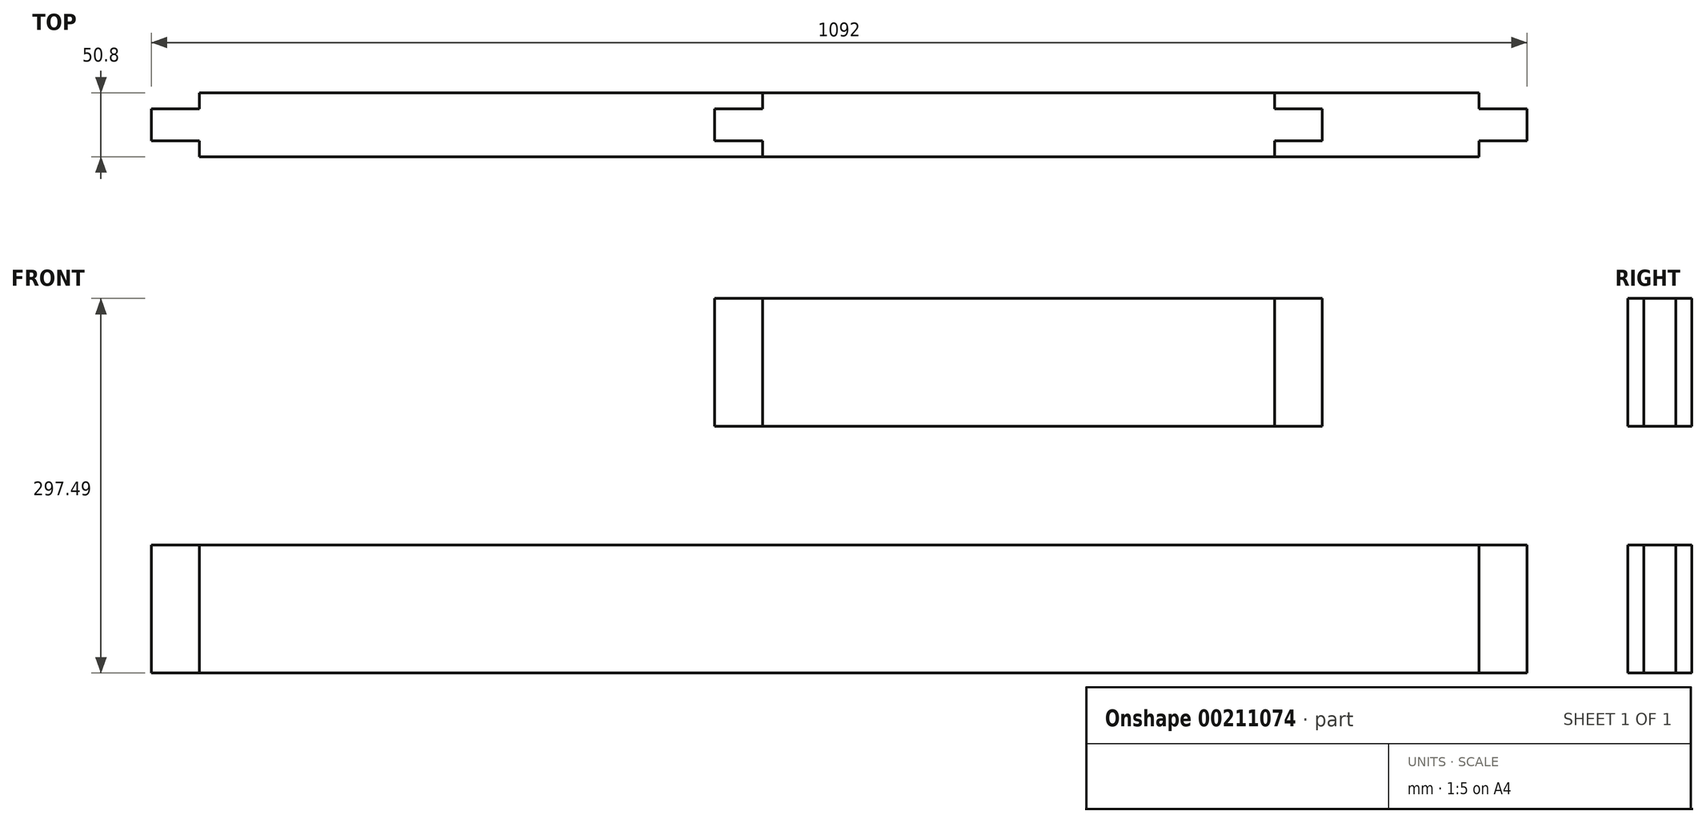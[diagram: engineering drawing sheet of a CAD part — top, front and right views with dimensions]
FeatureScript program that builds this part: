
annotation { "Feature Type Name" : "Feature", "Feature Type Description" : "" }
export const myFeature = defineFeature(function(context is Context, id is Id, definition is map)
    precondition{}
    {
        {
            var Q0;
            Q0=qCreatedBy(makeId("Front.planeOp"),FACE);
            var sketch = newSketch(context, id + "F0", { "sketchPlane" : qUnion([Q0])});
            skLineSegment(sketch, "E0.bottom", {"start": v(365.66, 0) * mm, "end": v(-650.34, 0) * mm});
            skLineSegment(sketch, "E0.top", {"start": v(365.66, 101.6) * mm, "end": v(-650.34, 101.6) * mm});
            skLineSegment(sketch, "E0.left", {"start": v(365.66, 0) * mm, "end": v(365.66, 101.6) * mm});
            skLineSegment(sketch, "E0.right", {"start": v(-650.34, 0) * mm, "end": v(-650.34, 101.6) * mm});
            skLineSegment(sketch, "E1.bottom", {"start": v(203.2, 195.9) * mm, "end": v(-203.2, 195.9) * mm});
            skLineSegment(sketch, "E1.top", {"start": v(203.2, 297.5) * mm, "end": v(-203.2, 297.5) * mm});
            skLineSegment(sketch, "E1.left", {"start": v(203.2, 195.9) * mm, "end": v(203.2, 297.5) * mm});
            skLineSegment(sketch, "E1.right", {"start": v(-203.2, 195.9) * mm, "end": v(-203.2, 297.5) * mm});
            skPoint(sketch, "E1.middle", {"position": v(0, 246.7) * mm});
            skSolve(sketch);
        }
        {
            var Q0;
            Q0=qSketchRegion(id+"F0",true);
            extrude(context, id + "F9", {"entities" : qUnion([Q0]), "depth" : 50.8 * mm});
        }
        {
            var Q0;
            Q0=makeQuery(id+"F9.opExtrude","SWEPT_FACE",FACE,{"disambiguationData":[OSD([sQuery(id+"F0.wireOp",EDGE,"E0.left")])]});
            var sketch = newSketch(context, id + "F1", { "sketchPlane" : qUnion([Q0])});
            skLineSegment(sketch, "E2.bottom", {"start": v(-12.7, 101.6) * mm, "end": v(-38.1, 101.6) * mm});
            skLineSegment(sketch, "E2.top", {"start": v(-12.7, 0) * mm, "end": v(-38.1, 0) * mm});
            skLineSegment(sketch, "E2.left", {"start": v(-12.7, 101.6) * mm, "end": v(-12.7, 0) * mm});
            skLineSegment(sketch, "E2.right", {"start": v(-38.1, 101.6) * mm, "end": v(-38.1, 0) * mm});
            skPoint(sketch, "E2.middle", {"position": v(-25.4, 50.8) * mm});
            skPoint(sketch, "E2.middle.positionSnap0", {"position": v(-25.4, 0) * mm});
            skPoint(sketch, "E2.middle.positionSnap1", {"position": v(0, 50.8) * mm});
            skPoint(sketch, "E2.centerSnap0", {"position": v(-25.4, 0) * mm});
            skPoint(sketch, "E2.centerSnap1", {"position": v(0, 50.8) * mm});
            skSolve(sketch);
        }
        {
            var Q0;
            Q0=makeQuery(id+"F1.imprint","IMPRINT",FACE,{"disambiguationData":[TD([[makeQuery(id+"F1.imprint","IMPRINT",EDGE,{"derivedFrom":sQuery(id+"F1.wireOp",EDGE,"E2.bottom")}),-1.0]])]});
            extrude(context, id + "F2", {"entities" : qUnion([Q0]), "operationType" : NewBodyOperationType.ADD, "depth" : 38 * mm});
        }
        {
            var Q0;
            Q0=makeQuery(id+"F9.opExtrude","SWEPT_FACE",FACE,{"disambiguationData":[OSD([sQuery(id+"F0.wireOp",EDGE,"E0.right")])]});
            var sketch = newSketch(context, id + "F3", { "sketchPlane" : qUnion([Q0])});
            skLineSegment(sketch, "E3.bottom", {"start": v(12.7, 101.6) * mm, "end": v(38.1, 101.6) * mm});
            skLineSegment(sketch, "E3.top", {"start": v(12.7, 0) * mm, "end": v(38.1, 0) * mm});
            skLineSegment(sketch, "E3.left", {"start": v(12.7, 101.6) * mm, "end": v(12.7, 0) * mm});
            skLineSegment(sketch, "E3.right", {"start": v(38.1, 101.6) * mm, "end": v(38.1, 0) * mm});
            skPoint(sketch, "E3.middle", {"position": v(25.4, 50.8) * mm});
            skPoint(sketch, "E3.middle.positionSnap0", {"position": v(0, 50.8) * mm});
            skPoint(sketch, "E3.middle.positionSnap1", {"position": v(25.4, 101.6) * mm});
            skPoint(sketch, "E3.centerSnap0", {"position": v(0, 50.8) * mm});
            skPoint(sketch, "E3.centerSnap1", {"position": v(25.4, 101.6) * mm});
            skSolve(sketch);
        }
        {
            var Q0;
            Q0=makeQuery(id+"F3.imprint","IMPRINT",FACE,{"disambiguationData":[TD([[makeQuery(id+"F3.imprint","IMPRINT",EDGE,{"derivedFrom":sQuery(id+"F3.wireOp",EDGE,"E3.bottom")}),1.0]])]});
            extrude(context, id + "F4", {"entities" : qUnion([Q0]), "operationType" : NewBodyOperationType.ADD, "depth" : 38 * mm});
        }
        {
            var Q0;
            Q0=makeQuery(id+"F9.opExtrude","SWEPT_FACE",FACE,{"disambiguationData":[OSD([sQuery(id+"F0.wireOp",EDGE,"E1.left")])]});
            var sketch = newSketch(context, id + "F5", { "sketchPlane" : qUnion([Q0])});
            skLineSegment(sketch, "E4.bottom", {"start": v(-38.1, 297.5) * mm, "end": v(-12.7, 297.5) * mm});
            skLineSegment(sketch, "E4.top", {"start": v(-38.1, 195.9) * mm, "end": v(-12.7, 195.9) * mm});
            skLineSegment(sketch, "E4.left", {"start": v(-38.1, 297.5) * mm, "end": v(-38.1, 195.9) * mm});
            skLineSegment(sketch, "E4.right", {"start": v(-12.7, 297.5) * mm, "end": v(-12.7, 195.9) * mm});
            skPoint(sketch, "E4.middle", {"position": v(-25.4, 246.7) * mm});
            skPoint(sketch, "E4.middle.positionSnap0", {"position": v(0, 246.7) * mm});
            skPoint(sketch, "E4.middle.positionSnap1", {"position": v(-25.4, 297.5) * mm});
            skPoint(sketch, "E4.centerSnap0", {"position": v(0, 246.7) * mm});
            skPoint(sketch, "E4.centerSnap1", {"position": v(-25.4, 297.5) * mm});
            skSolve(sketch);
        }
        {
            var Q0;
            Q0=makeQuery(id+"F9.opExtrude","SWEPT_FACE",FACE,{"disambiguationData":[OSD([sQuery(id+"F0.wireOp",EDGE,"E1.right")])]});
            var sketch = newSketch(context, id + "F6", { "sketchPlane" : qUnion([Q0])});
            skLineSegment(sketch, "E5.bottom", {"start": v(12.7, 297.5) * mm, "end": v(38.1, 297.5) * mm});
            skLineSegment(sketch, "E5.top", {"start": v(12.7, 195.9) * mm, "end": v(38.1, 195.9) * mm});
            skLineSegment(sketch, "E5.left", {"start": v(12.7, 297.5) * mm, "end": v(12.7, 195.9) * mm});
            skLineSegment(sketch, "E5.right", {"start": v(38.1, 297.5) * mm, "end": v(38.1, 195.9) * mm});
            skPoint(sketch, "E5.middle", {"position": v(25.4, 246.7) * mm});
            skPoint(sketch, "E5.middle.positionSnap0", {"position": v(25.4, 297.5) * mm});
            skPoint(sketch, "E5.middle.positionSnap1", {"position": v(0, 246.7) * mm});
            skPoint(sketch, "E5.centerSnap0", {"position": v(25.4, 297.5) * mm});
            skPoint(sketch, "E5.centerSnap1", {"position": v(0, 246.7) * mm});
            skSolve(sketch);
        }
        {
            var Q0;
            Q0=makeQuery(id+"F6.imprint","IMPRINT",FACE,{"disambiguationData":[TD([[makeQuery(id+"F6.imprint","IMPRINT",EDGE,{"derivedFrom":sQuery(id+"F6.wireOp",EDGE,"E5.bottom")}),1.0]])]});
            extrude(context, id + "F7", {"entities" : qUnion([Q0]), "operationType" : NewBodyOperationType.ADD, "depth" : 38 * mm});
        }
        {
            var Q0;
            Q0=makeQuery(id+"F5.imprint","IMPRINT",FACE,{"disambiguationData":[TD([[makeQuery(id+"F5.imprint","IMPRINT",EDGE,{"derivedFrom":sQuery(id+"F5.wireOp",EDGE,"E4.bottom")}),-1.0]])]});
            extrude(context, id + "F8", {"entities" : qUnion([Q0]), "operationType" : NewBodyOperationType.ADD, "depth" : 38 * mm});
        }
    });
